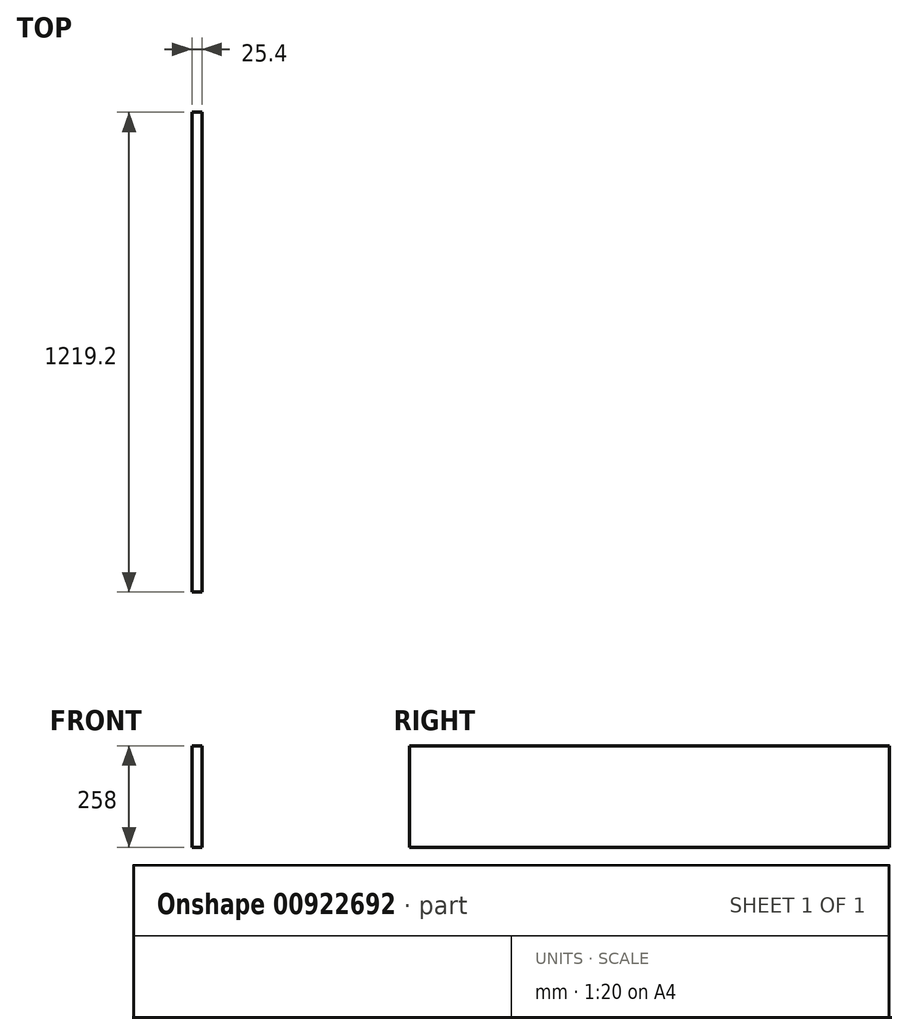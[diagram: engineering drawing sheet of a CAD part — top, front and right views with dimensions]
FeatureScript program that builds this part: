
annotation { "Feature Type Name" : "Feature", "Feature Type Description" : "" }
export const myFeature = defineFeature(function(context is Context, id is Id, definition is map)
    precondition{}
    {
        {
            var Q0;
            Q0=qCreatedBy(makeId("Right.planeOp"),FACE);
            var sketch = newSketch(context, id + "F0", { "sketchPlane" : qUnion([Q0])});
            skLineSegment(sketch, "E0.bottom", {"start": v(-550, -358) * mm, "end": v(669.2, -358) * mm});
            skLineSegment(sketch, "E0.top", {"start": v(-550, -100) * mm, "end": v(669.2, -100) * mm});
            skLineSegment(sketch, "E0.left", {"start": v(-550, -358) * mm, "end": v(-550, -100) * mm});
            skLineSegment(sketch, "E0.right", {"start": v(669.2, -358) * mm, "end": v(669.2, -100) * mm});
            skSolve(sketch);
        }
        {
            var Q0;
            Q0=makeQuery(id+"F0.imprint","IMPRINT",FACE,{"disambiguationData":[TD([[makeQuery(id+"F0.imprint","IMPRINT",EDGE,{"derivedFrom":sQuery(id+"F0.wireOp",EDGE,"E0.bottom")}),1.0]])]});
            extrude(context, id + "F1", {"entities" : qUnion([Q0]), "depth" : 25.4 * mm, "offsetDistance" : 25 * mm});
        }
    });
